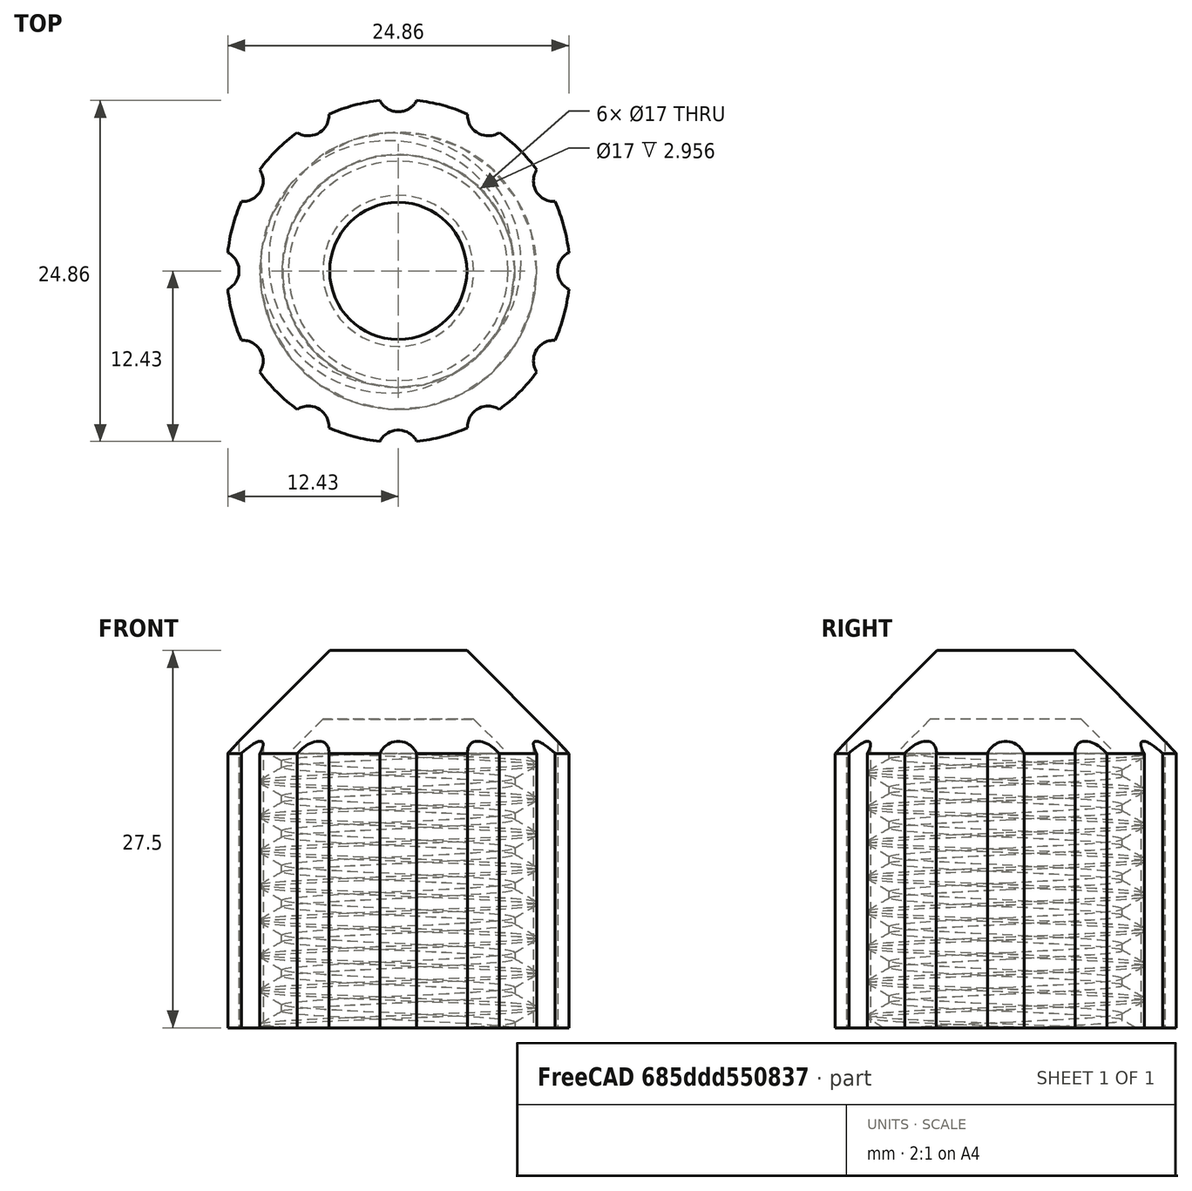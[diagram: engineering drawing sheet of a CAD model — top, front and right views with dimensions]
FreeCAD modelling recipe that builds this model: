
FCSTD DOCUMENT  (FreeCAD 0.19R)
Label: 0.75BoltCover
License: All rights reserved
LicenseURL: http://en.wikipedia.org/wiki/All_rights_reserved
objects: Sketcher::SketchObject×5, PartDesign::Pocket×2, PartDesign::Pad×1, PartDesign::SubtractiveHelix×1, PartDesign::Revolution×1, PartDesign::PolarPattern×1, PartDesign::Body×1, Mesh::Feature×1
note: 17 computed .brp shape members not serialized (recipe doc carries the construction recipe); baked Part::Feature solids carry a one-line shape summary decoded from their .brp

FEATURE [Sketcher::SketchObject] Sketch
  FullyConstrained = true
  MapMode = 5
  Support = -> [XY_Plane]
  sketch-geometry (2):
    g0: Circle CenterX=0 CenterY=0 CenterZ=0 NormalX=0 NormalY=0 NormalZ=1 AngleXU=0 Radius=12.5
    g1: Circle CenterX=0 CenterY=0 CenterZ=0 NormalX=0 NormalY=0 NormalZ=1 AngleXU=0 Radius=8.5
  constraints (4):
    c: Coincident(g0,g-1)
    c: Diameter(g0) = 25
    c: Coincident(g1,g0)
    c: Diameter(g1) = 17
FEATURE [PartDesign::Pad] Pad
  Direction = (1,1,1)
  Length = 20
  Length2 = 100
  Profile = -> Sketch
  Type = 0
FEATURE [Sketcher::SketchObject] Sketch001
  FullyConstrained = true
  MapMode = 5
  Placement = pos=(0,0,20) rot=(0,0,1;0rad)
  Support = -> [Pad]
  sketch-geometry (1):
    g0: Circle CenterX=0 CenterY=0 CenterZ=0 NormalX=0 NormalY=0 NormalZ=1 AngleXU=0 Radius=8.5
  constraints (2):
    c: Coincident(g0,g-1)
    c: Diameter(g0) = 17
FEATURE [PartDesign::Pocket] Pocket
  BaseFeature = -> Pad
  Length = 5
  Length2 = 100
  Profile = -> Sketch001
  Type = 1
FEATURE [Sketcher::SketchObject] Sketch002
  FullyConstrained = true
  MapMode = 5
  Placement = pos=(0,0,0) rot=(1,0,0;1.5708rad)
  Support = -> [XZ_Plane]
  sketch-geometry (4):
    g0: LineSegment StartX=8.36795 StartY=-2.2 StartZ=0 EndX=10.1 EndY=-1.2 EndZ=0
    g1: LineSegment StartX=10.1 StartY=-1.2 StartZ=0 EndX=10.1 EndY=-1 EndZ=0
    g2: LineSegment StartX=10.1 StartY=-1 StartZ=0 EndX=8.36795 EndY=1e-16 EndZ=0
    g3: LineSegment StartX=8.36795 StartY=-2.2 StartZ=0 EndX=8.36795 EndY=0 EndZ=0
  constraints (12):
    c: Coincident(g0,g1)
    c: Vertical(g1)
    c: Coincident(g1,g2)
    c: Angle(g2) = 2.61799
    c: Angle(g0) = 0.523599
    c: Distance(g1) = 0.2
    c: DistanceX(g1) = 10.1
    c: Coincident(g3,g0)
    c: Coincident(g3,g2)
    c: Vertical(g3)
    c: Distance(g2) = 2
    c: PointOnObject(g2,g-1)
FEATURE [PartDesign::SubtractiveHelix] SubtractiveHelix
  Angle = 0
  Axis = (0,-2e-16,1)
  Base = (0,0,0)
  BaseFeature = -> Pocket
  HasBeenEdited = true
  Height = 29.24
  LeftHanded = false
  Mode = 0
  Outside = false
  Pitch = 2.54
  Profile = -> Sketch002
  ReferenceAxis = -> Sketch002 [V_Axis]
  Turns = 11.5118
FEATURE [Sketcher::SketchObject] Sketch003
  FullyConstrained = true
  MapMode = 5
  Placement = pos=(0,0,0) rot=(0.57735,0.57735,0.57735;2.0944rad)
  Support = -> [YZ_Plane]
  sketch-geometry (6):
    g0: LineSegment StartX=8 StartY=20 StartZ=0 EndX=12.5 EndY=20 EndZ=0
    g1: LineSegment StartX=12.5 StartY=20 StartZ=0 EndX=5 EndY=27.5 EndZ=0
    g2: LineSegment StartX=5 StartY=27.5 StartZ=0 EndX=0 EndY=27.5 EndZ=0
    g3: LineSegment StartX=0 StartY=27.5 StartZ=0 EndX=0 EndY=22.5 EndZ=0
    g4: LineSegment StartX=0 StartY=22.5 StartZ=0 EndX=5.5 EndY=22.5 EndZ=0
    g5: LineSegment StartX=5.5 StartY=22.5 StartZ=0 EndX=8 EndY=20 EndZ=0
  constraints (18):
    c: Horizontal(g0)
    c: Coincident(g0,g1)
    c: Coincident(g1,g2)
    c: PointOnObject(g2,g-2)
    c: Coincident(g2,g3)
    c: PointOnObject(g3,g-2)
    c: Coincident(g3,g4)
    c: Horizontal(g4)
    c: DistanceY(g0) = 20
    c: Coincident(g4,g5)
    c: Coincident(g5,g0)
    c: Horizontal(g2)
    c: Angle(g1) = 2.35619
    c: Parallel(g5,g1)
    c: DistanceX(g0) = 8
    c: Distance(g3) = 5
    c: DistanceX(g0) = 12.5
    c: Distance(g2) = 5
FEATURE [PartDesign::Revolution] Revolution
  Angle = 360
  Axis = (-2e-16,3e-16,1)
  Base = (0,0,0)
  BaseFeature = -> SubtractiveHelix
  Profile = -> Sketch003
  ReferenceAxis = -> Sketch003 [V_Axis]
  Reversed = true
FEATURE [Sketcher::SketchObject] Sketch004
  FullyConstrained = false
  MapMode = 5
  Placement = pos=(0,0,0) rot=(1,0,0;3.14159rad)
  Support = -> [Revolution]
  sketch-geometry (1):
    g0: Circle CenterX=0 CenterY=13.1065 CenterZ=0 NormalX=0 NormalY=0 NormalZ=1 AngleXU=0 Radius=1.5
  constraints (2):
    c: PointOnObject(g0,g-2)
    c: Diameter(g0) = 3
FEATURE [PartDesign::Pocket] Pocket001
  BaseFeature = -> Revolution
  Length = 5
  Length2 = 100
  Profile = -> Sketch004
  Type = 1
FEATURE [PartDesign::PolarPattern] PolarPattern
  Angle = 360
  Axis = -> Sketch004 [N_Axis]
  BaseFeature = -> Pocket001
  Occurrences = 12
  Originals = -> [Pocket001]
FEATURE [PartDesign::Body] Body
  Group = -> [Sketch,Pad,Sketch001,Pocket,Sketch002,SubtractiveHelix,Sketch003,Revolution,Sketch004,Pocket001,PolarPattern]
  Origin = -> Origin
  Tip = -> PolarPattern
FEATURE [Mesh::Feature] Mesh  label="PolarPattern (Meshed)"
